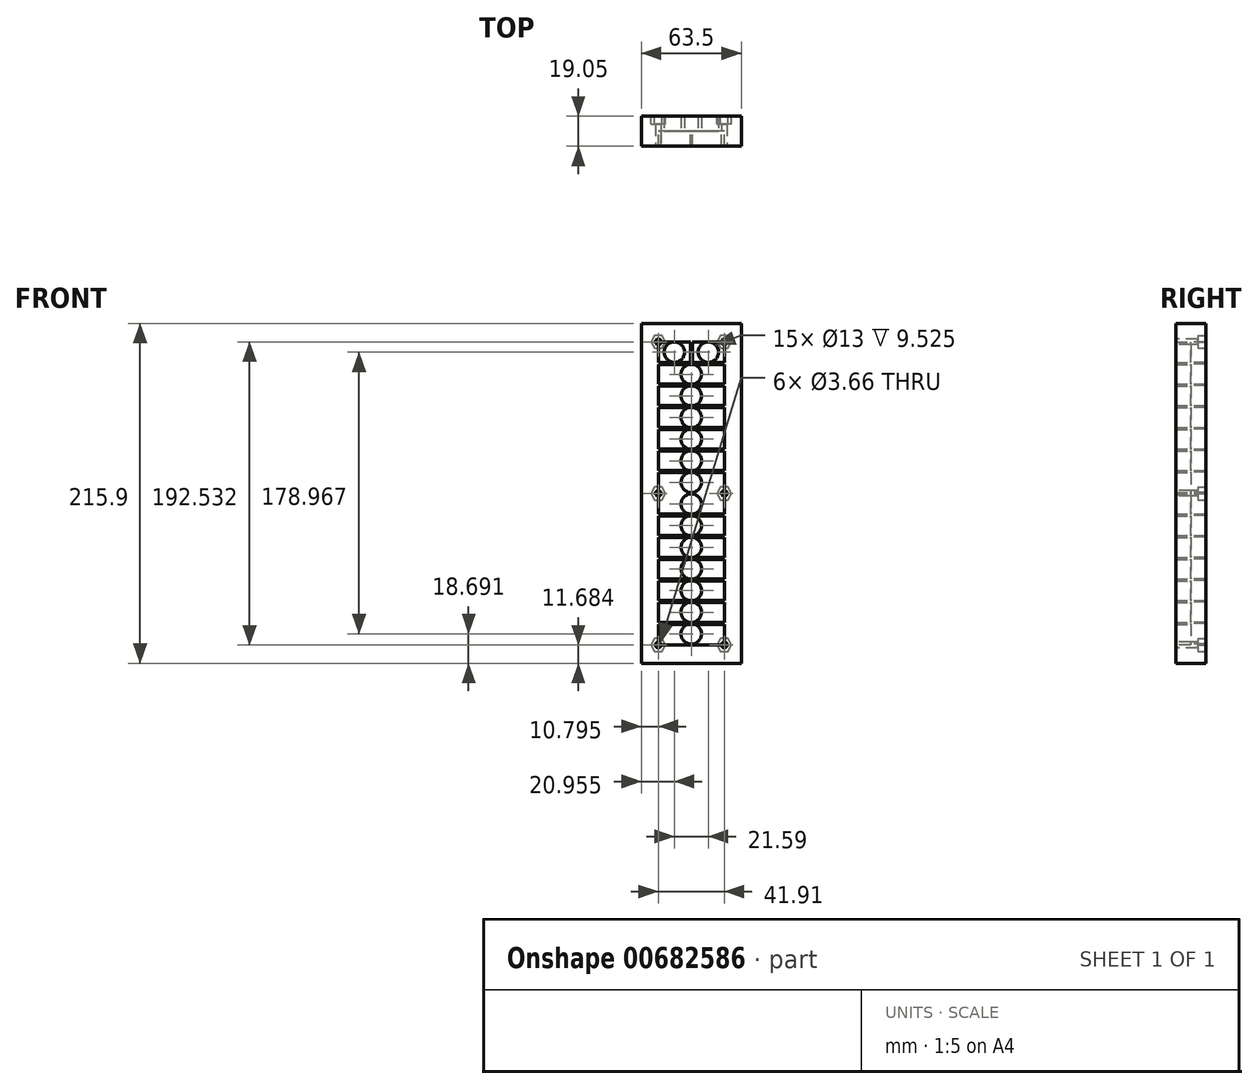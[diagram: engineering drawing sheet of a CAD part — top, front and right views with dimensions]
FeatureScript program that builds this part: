
annotation { "Feature Type Name" : "Feature", "Feature Type Description" : "" }
export const myFeature = defineFeature(function(context is Context, id is Id, definition is map)
    precondition{}
    {
        {
            var Q0;
            Q0=qCreatedBy(makeId("Front.planeOp"),FACE);
            var sketch = newSketch(context, id + "F0", { "sketchPlane" : qUnion([Q0])});
            skLineSegment(sketch, "E0.bottom", {"start": v(31.75, 107.95) * mm, "end": v(-31.75, 107.95) * mm});
            skLineSegment(sketch, "E0.top", {"start": v(31.75, -107.95) * mm, "end": v(-31.75, -107.95) * mm});
            skLineSegment(sketch, "E0.left", {"start": v(31.75, 107.95) * mm, "end": v(31.75, -107.95) * mm});
            skLineSegment(sketch, "E0.right", {"start": v(-31.75, 107.95) * mm, "end": v(-31.75, -107.95) * mm});
            skPoint(sketch, "E0.middle", {"position": v(0, 0) * mm});
            skSolve(sketch);
        }
        {
            var Q0;
            Q0=makeQuery(id+"F0.imprint","IMPRINT",FACE,{"disambiguationData":[TD([[makeQuery(id+"F0.imprint","IMPRINT",EDGE,{"derivedFrom":sQuery(id+"F0.wireOp",EDGE,"E0.bottom")}),1.0]])]});
            extrude(context, id + "F1", {"entities" : qUnion([Q0]), "depth" : 19.05 * mm, "offsetDistance" : 25.4 * mm});
        }
        {
            var Q0;
            Q0=makeQuery(id+"F1.opExtrude","CAP_FACE",FACE,{"disambiguationData":[OSD([sQuery(id+"F0.wireOp",EDGE,"E0.bottom"),sQuery(id+"F0.wireOp",EDGE,"E0.top"),sQuery(id+"F0.wireOp",EDGE,"E0.left"),sQuery(id+"F0.wireOp",EDGE,"E0.right")])],"isStart":false});
            var sketch = newSketch(context, id + "F2", { "sketchPlane" : qUnion([Q0])});
            skLineSegment(sketch, "E1.bottom", {"start": v(20.96, 96.27) * mm, "end": v(-20.95, 96.27) * mm});
            skLineSegment(sketch, "E1.top", {"start": v(20.95, -96.27) * mm, "end": v(-20.96, -96.27) * mm});
            skLineSegment(sketch, "E1.left", {"start": v(20.96, 96.27) * mm, "end": v(20.95, -96.27) * mm});
            skLineSegment(sketch, "E1.right", {"start": v(-20.95, 96.27) * mm, "end": v(-20.96, -96.27) * mm});
            skPoint(sketch, "E1.middle", {"position": v(0, 0) * mm});
            skSolve(sketch);
        }
        {
            var Q0;
            Q0 = qSketchRegion(id + "F2", true);
            extrude(context, id + "F3", {"entities" : qUnion([Q0]), "operationType" : NewBodyOperationType.REMOVE, "oppositeDirection" : true, "depth" : 9.52 * mm, "offsetDistance" : 25.4 * mm});
        }
        {
            var Q0;
            Q0=makeQuery(id+"F1.opExtrude","CAP_FACE",FACE,{"disambiguationData":[OSD([sQuery(id+"F0.wireOp",EDGE,"E0.bottom"),sQuery(id+"F0.wireOp",EDGE,"E0.top"),sQuery(id+"F0.wireOp",EDGE,"E0.left"),sQuery(id+"F0.wireOp",EDGE,"E0.right")])],"isStart":false});
            var sketch = newSketch(context, id + "F4", { "sketchPlane" : qUnion([Q0])});
            skPoint(sketch, "E2", {"position": v(-20.95, 96.27) * mm});
            skPoint(sketch, "E3", {"position": v(20.96, 96.27) * mm});
            skPoint(sketch, "E4", {"position": v(-20.96, -96.27) * mm});
            skPoint(sketch, "E5", {"position": v(20.95, -96.27) * mm});
            skPoint(sketch, "E6", {"position": v(-20.96, 0) * mm});
            skPoint(sketch, "E7", {"position": v(20.96, 0) * mm});
            skSolve(sketch);
        }
        {
            var Q0;
            Q0=sQuery(id+"F4.wireOp",VERTEX,"E4");
            var Q1;
            Q1=sQuery(id+"F4.wireOp",VERTEX,"E6");
            var Q2;
            Q2=sQuery(id+"F4.wireOp",VERTEX,"E7");
            var Q3;
            Q3=sQuery(id+"F4.wireOp",VERTEX,"E5");
            var Q4;
            Q4=sQuery(id+"F4.wireOp",VERTEX,"E2");
            var Q5;
            Q5=sQuery(id+"F4.wireOp",VERTEX,"E3");
            var Q6;
            Q6=makeQuery(id+"F1.opExtrude","SWEPT_BODY",BODY,{"disambiguationData":[OSD([sQuery(id+"F0.wireOp",EDGE,"E0.bottom"),sQuery(id+"F0.wireOp",EDGE,"E0.top"),sQuery(id+"F0.wireOp",EDGE,"E0.left"),sQuery(id+"F0.wireOp",EDGE,"E0.right")])]});
            hole(context, id + "F5", {"style" : HoleStyle.SIMPLE, "endStyle" : HoleEndStyle.BLIND, "standardTappedOrClearance" : lookupTablePath({ "standard" : "ANSI", "fit" : "Close", "size" : "#6", "type" : "Clearance" }), "standardBlindInLast" : lookupTablePath({ "fit" : "Close", "standard" : "ANSI", "size" : "#6", "type" : "Clearance" }), "holeDiameter" : 3.66 * mm, "majorDiameter" : 6.35 * mm, "holeDepth" : 19.05 * mm, "isTappedThrough" : true, "tappedDepth" : 12.7 * mm, "tapClearance" : 3, "locations" : qUnion([Q0, Q1, Q2, Q3, Q4, Q5]), "scope" : qUnion([Q6])});
        }
        {
            var Q0;
            Q0=makeQuery(id+"F1.opExtrude","CAP_FACE",FACE,{"disambiguationData":[OSD([sQuery(id+"F0.wireOp",EDGE,"E0.bottom"),sQuery(id+"F0.wireOp",EDGE,"E0.top"),sQuery(id+"F0.wireOp",EDGE,"E0.left"),sQuery(id+"F0.wireOp",EDGE,"E0.right")])],"isStart":true});
            var sketch = newSketch(context, id + "F6", { "sketchPlane" : qUnion([Q0])});
            skCircle(sketch, "E8.cCircle", {"center": v(-20.96, 96.27) * mm, "radius": 4.06 * mm, "construction": true});
            skLineSegment(sketch, "E8.0", {"start": v(-18.6, 100.33) * mm, "end": v(-16.26, 96.27) * mm});
            skLineSegment(sketch, "E8.1", {"start": v(-16.26, 96.27) * mm, "end": v(-18.6, 92.2) * mm});
            skLineSegment(sketch, "E8.2", {"start": v(-18.6, 92.2) * mm, "end": v(-23.3, 92.2) * mm});
            skLineSegment(sketch, "E8.3", {"start": v(-23.3, 92.2) * mm, "end": v(-25.65, 96.27) * mm});
            skLineSegment(sketch, "E8.4", {"start": v(-25.65, 96.27) * mm, "end": v(-23.3, 100.33) * mm});
            skLineSegment(sketch, "E8.5", {"start": v(-23.3, 100.33) * mm, "end": v(-18.6, 100.33) * mm});
            skPoint(sketch, "E8.0.midPoint", {"position": v(-17.44, 98.3) * mm});
            skLineSegment(sketch, "E9.0.1.0", {"start": v(-16.26, 0) * mm, "end": v(-18.6, -4.06) * mm});
            skLineSegment(sketch, "E9.0.1.1", {"start": v(-18.6, -4.06) * mm, "end": v(-23.3, -4.06) * mm});
            skLineSegment(sketch, "E9.0.1.2", {"start": v(-23.3, -4.06) * mm, "end": v(-25.65, 0) * mm});
            skLineSegment(sketch, "E9.0.1.3", {"start": v(-25.65, 0) * mm, "end": v(-23.3, 4.06) * mm});
            skLineSegment(sketch, "E9.0.1.4", {"start": v(-23.3, 4.06) * mm, "end": v(-18.6, 4.06) * mm});
            skLineSegment(sketch, "E9.0.1.5", {"start": v(-18.6, 4.06) * mm, "end": v(-16.26, 0) * mm});
            skLineSegment(sketch, "E9.0.2.0", {"start": v(-16.26, -96.27) * mm, "end": v(-18.6, -100.33) * mm});
            skLineSegment(sketch, "E9.0.2.1", {"start": v(-18.6, -100.33) * mm, "end": v(-23.3, -100.33) * mm});
            skLineSegment(sketch, "E9.0.2.2", {"start": v(-23.3, -100.33) * mm, "end": v(-25.65, -96.27) * mm});
            skLineSegment(sketch, "E9.0.2.3", {"start": v(-25.65, -96.27) * mm, "end": v(-23.3, -92.2) * mm});
            skLineSegment(sketch, "E9.0.2.4", {"start": v(-23.3, -92.2) * mm, "end": v(-18.6, -92.2) * mm});
            skLineSegment(sketch, "E9.0.2.5", {"start": v(-18.6, -92.2) * mm, "end": v(-16.26, -96.27) * mm});
            skLineSegment(sketch, "E9.1.0.0", {"start": v(25.65, 96.27) * mm, "end": v(23.3, 92.2) * mm});
            skLineSegment(sketch, "E9.1.0.1", {"start": v(23.3, 92.2) * mm, "end": v(18.6, 92.2) * mm});
            skLineSegment(sketch, "E9.1.0.2", {"start": v(18.6, 92.2) * mm, "end": v(16.26, 96.27) * mm});
            skLineSegment(sketch, "E9.1.0.3", {"start": v(16.26, 96.27) * mm, "end": v(18.6, 100.33) * mm});
            skLineSegment(sketch, "E9.1.0.4", {"start": v(18.6, 100.33) * mm, "end": v(23.3, 100.33) * mm});
            skLineSegment(sketch, "E9.1.0.5", {"start": v(23.3, 100.33) * mm, "end": v(25.65, 96.27) * mm});
            skLineSegment(sketch, "E9.1.1.0", {"start": v(25.65, 0) * mm, "end": v(23.3, -4.06) * mm});
            skLineSegment(sketch, "E9.1.1.1", {"start": v(23.3, -4.06) * mm, "end": v(18.6, -4.06) * mm});
            skLineSegment(sketch, "E9.1.1.2", {"start": v(18.6, -4.06) * mm, "end": v(16.26, 0) * mm});
            skLineSegment(sketch, "E9.1.1.3", {"start": v(16.26, 0) * mm, "end": v(18.6, 4.06) * mm});
            skLineSegment(sketch, "E9.1.1.4", {"start": v(18.6, 4.06) * mm, "end": v(23.3, 4.06) * mm});
            skLineSegment(sketch, "E9.1.1.5", {"start": v(23.3, 4.06) * mm, "end": v(25.65, 0) * mm});
            skLineSegment(sketch, "E9.1.2.0", {"start": v(25.65, -96.27) * mm, "end": v(23.3, -100.33) * mm});
            skLineSegment(sketch, "E9.1.2.1", {"start": v(23.3, -100.33) * mm, "end": v(18.6, -100.33) * mm});
            skLineSegment(sketch, "E9.1.2.2", {"start": v(18.6, -100.33) * mm, "end": v(16.26, -96.27) * mm});
            skLineSegment(sketch, "E9.1.2.3", {"start": v(16.26, -96.27) * mm, "end": v(18.6, -92.2) * mm});
            skLineSegment(sketch, "E9.1.2.4", {"start": v(18.6, -92.2) * mm, "end": v(23.3, -92.2) * mm});
            skLineSegment(sketch, "E9.1.2.5", {"start": v(23.3, -92.2) * mm, "end": v(25.65, -96.27) * mm});
            skLineSegment(sketch, "E9.direction1", {"start": v(-18.6, 92.2) * mm, "end": v(23.3, 92.2) * mm, "construction": true});
            skLineSegment(sketch, "E9.direction2", {"start": v(-18.6, 92.2) * mm, "end": v(-18.6, -4.06) * mm, "construction": true});
            skSolve(sketch);
        }
        {
            var Q0;
            Q0=makeQuery(id+"F6.imprint","IMPRINT",FACE,{"disambiguationData":[TD([[makeQuery(id+"F6.imprint","IMPRINT",EDGE,{"derivedFrom":sQuery(id+"F6.wireOp",EDGE,"E8.0")}),-1.0]])]});
            var Q1;
            Q1=makeQuery(id+"F6.imprint","IMPRINT",FACE,{"disambiguationData":[TD([[makeQuery(id+"F6.imprint","IMPRINT",EDGE,{"derivedFrom":sQuery(id+"F6.wireOp",EDGE,"E9.1.0.0")}),-1.0]])]});
            var Q2;
            Q2=makeQuery(id+"F6.imprint","IMPRINT",FACE,{"disambiguationData":[TD([[makeQuery(id+"F6.imprint","IMPRINT",EDGE,{"derivedFrom":sQuery(id+"F6.wireOp",EDGE,"E9.0.1.0")}),-1.0]])]});
            var Q3;
            Q3=makeQuery(id+"F6.imprint","IMPRINT",FACE,{"disambiguationData":[TD([[makeQuery(id+"F6.imprint","IMPRINT",EDGE,{"derivedFrom":sQuery(id+"F6.wireOp",EDGE,"E9.1.1.0")}),-1.0]])]});
            var Q4;
            Q4=makeQuery(id+"F6.imprint","IMPRINT",FACE,{"disambiguationData":[TD([[makeQuery(id+"F6.imprint","IMPRINT",EDGE,{"derivedFrom":sQuery(id+"F6.wireOp",EDGE,"E9.0.2.0")}),-1.0]])]});
            var Q5;
            Q5=makeQuery(id+"F6.imprint","IMPRINT",FACE,{"disambiguationData":[TD([[makeQuery(id+"F6.imprint","IMPRINT",EDGE,{"derivedFrom":sQuery(id+"F6.wireOp",EDGE,"E9.1.2.0")}),-1.0]])]});
            extrude(context, id + "F7", {"entities" : qUnion([Q0, Q1, Q2, Q3, Q4, Q5]), "operationType" : NewBodyOperationType.REMOVE, "oppositeDirection" : true, "depth" : 5.08 * mm, "offsetDistance" : 25.4 * mm});
        }
        {
            var Q0;
            Q0=makeQuery(id+"F3.boolean.opBoolean","COPY",FACE,{"derivedFrom":makeQuery(id+"F3.opExtrude","CAP_FACE",FACE,{"disambiguationData":[OSD([sQuery(id+"F2.wireOp",EDGE,"E1.bottom"),sQuery(id+"F2.wireOp",EDGE,"E1.top"),sQuery(id+"F2.wireOp",EDGE,"E1.left"),sQuery(id+"F2.wireOp",EDGE,"E1.right")])],"isStart":false})});
            var sketch = newSketch(context, id + "F8", { "sketchPlane" : qUnion([Q0])});
            skLineSegment(sketch, "E10.bottom", {"start": v(20.96, 0.64) * mm, "end": v(-20.96, 0.64) * mm});
            skLineSegment(sketch, "E10.top", {"start": v(20.96, -0.64) * mm, "end": v(-20.96, -0.64) * mm});
            skLineSegment(sketch, "E10.left", {"start": v(20.96, 0.64) * mm, "end": v(20.96, -0.64) * mm});
            skLineSegment(sketch, "E10.right", {"start": v(-20.96, 0.64) * mm, "end": v(-20.96, -0.64) * mm});
            skPoint(sketch, "E10.middle", {"position": v(0, 0) * mm});
            skLineSegment(sketch, "E11.0.1.0", {"start": v(20.96, 13.12) * mm, "end": v(-20.96, 13.12) * mm});
            skLineSegment(sketch, "E11.0.1.1", {"start": v(20.96, 14.39) * mm, "end": v(20.96, 13.12) * mm});
            skLineSegment(sketch, "E11.0.1.2", {"start": v(20.96, 14.39) * mm, "end": v(-20.96, 14.39) * mm});
            skLineSegment(sketch, "E11.0.1.3", {"start": v(-20.96, 14.39) * mm, "end": v(-20.96, 13.12) * mm});
            skLineSegment(sketch, "E11.0.2.0", {"start": v(20.96, 26.87) * mm, "end": v(-20.96, 26.87) * mm});
            skLineSegment(sketch, "E11.0.2.1", {"start": v(20.96, 28.14) * mm, "end": v(20.96, 26.87) * mm});
            skLineSegment(sketch, "E11.0.2.2", {"start": v(20.96, 28.14) * mm, "end": v(-20.96, 28.14) * mm});
            skLineSegment(sketch, "E11.0.2.3", {"start": v(-20.96, 28.14) * mm, "end": v(-20.96, 26.87) * mm});
            skLineSegment(sketch, "E11.0.3.0", {"start": v(20.96, 40.62) * mm, "end": v(-20.96, 40.62) * mm});
            skLineSegment(sketch, "E11.0.3.1", {"start": v(20.96, 41.9) * mm, "end": v(20.96, 40.62) * mm});
            skLineSegment(sketch, "E11.0.3.2", {"start": v(20.96, 41.9) * mm, "end": v(-20.96, 41.9) * mm});
            skLineSegment(sketch, "E11.0.3.3", {"start": v(-20.96, 41.9) * mm, "end": v(-20.96, 40.62) * mm});
            skLineSegment(sketch, "E11.0.4.0", {"start": v(20.96, 54.37) * mm, "end": v(-20.96, 54.37) * mm});
            skLineSegment(sketch, "E11.0.4.1", {"start": v(20.96, 55.64) * mm, "end": v(20.96, 54.37) * mm});
            skLineSegment(sketch, "E11.0.4.2", {"start": v(20.96, 55.64) * mm, "end": v(-20.96, 55.64) * mm});
            skLineSegment(sketch, "E11.0.4.3", {"start": v(-20.96, 55.64) * mm, "end": v(-20.96, 54.37) * mm});
            skLineSegment(sketch, "E11.0.5.0", {"start": v(20.96, 68.13) * mm, "end": v(-20.96, 68.13) * mm});
            skLineSegment(sketch, "E11.0.5.1", {"start": v(20.96, 69.4) * mm, "end": v(20.96, 68.13) * mm});
            skLineSegment(sketch, "E11.0.5.2", {"start": v(20.96, 69.4) * mm, "end": v(-20.96, 69.4) * mm});
            skLineSegment(sketch, "E11.0.5.3", {"start": v(-20.96, 69.4) * mm, "end": v(-20.96, 68.13) * mm});
            skLineSegment(sketch, "E11.0.6.0", {"start": v(20.96, 81.88) * mm, "end": v(-20.96, 81.88) * mm});
            skLineSegment(sketch, "E11.0.6.1", {"start": v(20.96, 83.15) * mm, "end": v(20.96, 81.88) * mm});
            skLineSegment(sketch, "E11.0.6.2", {"start": v(20.96, 83.15) * mm, "end": v(-20.96, 83.15) * mm});
            skLineSegment(sketch, "E11.0.6.3", {"start": v(-20.96, 83.15) * mm, "end": v(-20.96, 81.88) * mm});
            skLineSegment(sketch, "E11.direction1", {"start": v(-20.96, -0.64) * mm, "end": v(4.44, -0.64) * mm, "construction": true});
            skLineSegment(sketch, "E11.direction2", {"start": v(-20.96, -0.64) * mm, "end": v(-20.96, 13.12) * mm, "construction": true});
            skLineSegment(sketch, "E12", {"start": v(20.96, 0) * mm, "end": v(0, 0) * mm});
            skLineSegment(sketch, "E13.MirrorCS", {"start": v(-20.96, -14.39) * mm, "end": v(-20.96, -13.12) * mm});
            skLineSegment(sketch, "E14.MirrorCS", {"start": v(20.96, -14.39) * mm, "end": v(-20.96, -14.39) * mm});
            skLineSegment(sketch, "E15.MirrorCS", {"start": v(20.96, -13.12) * mm, "end": v(-20.96, -13.12) * mm});
            skLineSegment(sketch, "E16.MirrorCS", {"start": v(20.96, -14.39) * mm, "end": v(20.96, -13.12) * mm});
            skLineSegment(sketch, "E17.MirrorCS", {"start": v(20.96, -26.87) * mm, "end": v(-20.96, -26.87) * mm});
            skLineSegment(sketch, "E18.MirrorCS", {"start": v(20.96, -28.14) * mm, "end": v(-20.96, -28.14) * mm});
            skLineSegment(sketch, "E19.MirrorCS", {"start": v(20.96, -28.14) * mm, "end": v(20.96, -26.87) * mm});
            skLineSegment(sketch, "E20.MirrorCS", {"start": v(-20.96, -28.14) * mm, "end": v(-20.96, -26.87) * mm});
            skLineSegment(sketch, "E21.MirrorCS", {"start": v(20.96, -41.9) * mm, "end": v(-20.96, -41.9) * mm});
            skLineSegment(sketch, "E22.MirrorCS", {"start": v(20.96, -40.62) * mm, "end": v(-20.96, -40.62) * mm});
            skLineSegment(sketch, "E23.MirrorCS", {"start": v(-20.96, -41.9) * mm, "end": v(-20.96, -40.62) * mm});
            skLineSegment(sketch, "E24.MirrorCS", {"start": v(20.96, -41.9) * mm, "end": v(20.96, -40.62) * mm});
            skLineSegment(sketch, "E25.MirrorCS", {"start": v(20.96, -55.64) * mm, "end": v(-20.96, -55.64) * mm});
            skLineSegment(sketch, "E26.MirrorCS", {"start": v(20.96, -54.37) * mm, "end": v(-20.96, -54.37) * mm});
            skLineSegment(sketch, "E27.MirrorCS", {"start": v(-20.96, -55.64) * mm, "end": v(-20.96, -54.37) * mm});
            skLineSegment(sketch, "E28.MirrorCS", {"start": v(20.96, -55.64) * mm, "end": v(20.96, -54.37) * mm});
            skLineSegment(sketch, "E29.MirrorCS", {"start": v(20.96, -69.4) * mm, "end": v(-20.96, -69.4) * mm});
            skLineSegment(sketch, "E30.MirrorCS", {"start": v(20.96, -68.13) * mm, "end": v(-20.96, -68.13) * mm});
            skLineSegment(sketch, "E31.MirrorCS", {"start": v(-20.96, -69.4) * mm, "end": v(-20.96, -68.13) * mm});
            skLineSegment(sketch, "E32.MirrorCS", {"start": v(20.96, -69.4) * mm, "end": v(20.96, -68.13) * mm});
            skLineSegment(sketch, "E33.MirrorCS", {"start": v(20.96, -83.15) * mm, "end": v(-20.96, -83.15) * mm});
            skLineSegment(sketch, "E34.MirrorCS", {"start": v(20.96, -81.88) * mm, "end": v(-20.96, -81.88) * mm});
            skLineSegment(sketch, "E35.MirrorCS", {"start": v(20.96, -83.15) * mm, "end": v(20.96, -81.88) * mm});
            skLineSegment(sketch, "E36.MirrorCS", {"start": v(-20.96, -83.15) * mm, "end": v(-20.96, -81.88) * mm});
            skSolve(sketch);
        }
        {
            var Q0;
            Q0=makeQuery(id+"F8.imprint","IMPRINT",FACE,{"disambiguationData":[TD([[makeQuery(id+"F8.imprint","IMPRINT",EDGE,{"derivedFrom":sQuery(id+"F8.wireOp",EDGE,"E11.0.6.0")}),-1.0]])]});
            var Q1;
            Q1=makeQuery(id+"F8.imprint","IMPRINT",FACE,{"disambiguationData":[TD([[makeQuery(id+"F8.imprint","IMPRINT",EDGE,{"derivedFrom":sQuery(id+"F8.wireOp",EDGE,"E11.0.5.0")}),-1.0]])]});
            var Q2;
            Q2=makeQuery(id+"F8.imprint","IMPRINT",FACE,{"disambiguationData":[TD([[makeQuery(id+"F8.imprint","IMPRINT",EDGE,{"derivedFrom":sQuery(id+"F8.wireOp",EDGE,"E11.0.4.0")}),-1.0]])]});
            var Q3;
            Q3=makeQuery(id+"F8.imprint","IMPRINT",FACE,{"disambiguationData":[TD([[makeQuery(id+"F8.imprint","IMPRINT",EDGE,{"derivedFrom":sQuery(id+"F8.wireOp",EDGE,"E11.0.3.0")}),-1.0]])]});
            var Q4;
            Q4=makeQuery(id+"F8.imprint","IMPRINT",FACE,{"disambiguationData":[TD([[makeQuery(id+"F8.imprint","IMPRINT",EDGE,{"derivedFrom":sQuery(id+"F8.wireOp",EDGE,"E11.0.2.0")}),-1.0]])]});
            var Q5;
            Q5=makeQuery(id+"F8.imprint","IMPRINT",FACE,{"disambiguationData":[TD([[makeQuery(id+"F8.imprint","IMPRINT",EDGE,{"derivedFrom":sQuery(id+"F8.wireOp",EDGE,"E11.0.1.0")}),-1.0]])]});
            var Q6;
            {var subQ0=sQuery(id+"F8.wireOp",EDGE,"E10.bottom");var subQ1=makeQuery(id+"F3.boolean.opBoolean","COPY",FACE,{"derivedFrom":makeQuery(id+"F3.opExtrude","CAP_FACE",FACE,{"disambiguationData":[OSD([sQuery(id+"F2.wireOp",EDGE,"E1.bottom"),sQuery(id+"F2.wireOp",EDGE,"E1.top"),sQuery(id+"F2.wireOp",EDGE,"E1.left"),sQuery(id+"F2.wireOp",EDGE,"E1.right")])],"isStart":false})});var subQ2=makeQuery(id+"F5.hole-2.boolean.opBoolean","INTERSECT",EDGE,{"derivedFrom":[subQ1,makeQuery(id+"F5.hole-2.opRevolve","SWEPT_FACE",FACE,{"disambiguationData":[OSD([sQuery(id+"F5.hole-2.sketch.wireOp",EDGE,"core_line_2")])]})]});var subQ3=makeQuery(id+"F8.imprint","INTERSECT",VERTEX,{"derivedFrom":[subQ2,subQ0]});Q6=makeQuery(id+"F8.imprint","IMPRINT",FACE,{"disambiguationData":[TD([[makeQuery(id+"F8.imprint","IMPRINT",EDGE,{"disambiguationData":[TD([[subQ3,-1.0]])],"derivedFrom":subQ0}),1.0]])]});}
            var Q7;
            Q7=makeQuery(id+"F8.imprint","IMPRINT",FACE,{"disambiguationData":[TD([[makeQuery(id+"F8.imprint","IMPRINT",EDGE,{"derivedFrom":sQuery(id+"F8.wireOp",EDGE,"E13.MirrorCS")}),1.0]])]});
            var Q8;
            Q8=makeQuery(id+"F8.imprint","IMPRINT",FACE,{"disambiguationData":[TD([[makeQuery(id+"F8.imprint","IMPRINT",EDGE,{"derivedFrom":sQuery(id+"F8.wireOp",EDGE,"E17.MirrorCS")}),1.0]])]});
            var Q9;
            Q9=makeQuery(id+"F8.imprint","IMPRINT",FACE,{"disambiguationData":[TD([[makeQuery(id+"F8.imprint","IMPRINT",EDGE,{"derivedFrom":sQuery(id+"F8.wireOp",EDGE,"E21.MirrorCS")}),-1.0]])]});
            var Q10;
            Q10=makeQuery(id+"F8.imprint","IMPRINT",FACE,{"disambiguationData":[TD([[makeQuery(id+"F8.imprint","IMPRINT",EDGE,{"derivedFrom":sQuery(id+"F8.wireOp",EDGE,"E25.MirrorCS")}),-1.0]])]});
            var Q11;
            Q11=makeQuery(id+"F8.imprint","IMPRINT",FACE,{"disambiguationData":[TD([[makeQuery(id+"F8.imprint","IMPRINT",EDGE,{"derivedFrom":sQuery(id+"F8.wireOp",EDGE,"E29.MirrorCS")}),-1.0]])]});
            var Q12;
            Q12=makeQuery(id+"F8.imprint","IMPRINT",FACE,{"disambiguationData":[TD([[makeQuery(id+"F8.imprint","IMPRINT",EDGE,{"derivedFrom":sQuery(id+"F8.wireOp",EDGE,"E33.MirrorCS")}),-1.0]])]});
            var Q13;
            Q13=makeQuery(id+"F1.opExtrude","CAP_FACE",FACE,{"disambiguationData":[OSD([sQuery(id+"F0.wireOp",EDGE,"E0.bottom"),sQuery(id+"F0.wireOp",EDGE,"E0.top"),sQuery(id+"F0.wireOp",EDGE,"E0.left"),sQuery(id+"F0.wireOp",EDGE,"E0.right")])],"isStart":false});
            extrude(context, id + "F9", {"entities" : qUnion([Q0, Q1, Q2, Q3, Q4, Q5, Q6, Q7, Q8, Q9, Q10, Q11, Q12]), "operationType" : NewBodyOperationType.ADD, "endBound" : BoundingType.UP_TO_SURFACE, "depth" : 25.4 * mm, "endBoundEntityFace" : qUnion([Q13]), "offsetDistance" : 25.4 * mm});
        }
        {
            var Q0;
            {var subQ0=sQuery(id+"F2.wireOp",EDGE,"E1.right");var subQ1=sQuery(id+"F2.wireOp",EDGE,"E1.left");var subQ2=sQuery(id+"F2.wireOp",EDGE,"E1.bottom");Q0=makeQuery(id+"F9.boolean.opBoolean","SPLIT",FACE,{"disambiguationData":[TD([makeQuery(id+"F3.boolean.opBoolean","COPY",FACE,{"derivedFrom":makeQuery(id+"F3.opExtrude","SWEPT_FACE",FACE,{"disambiguationData":[OSD([subQ2])]})})])],"derivedFrom":makeQuery(id+"F3.boolean.opBoolean","COPY",FACE,{"derivedFrom":makeQuery(id+"F3.opExtrude","CAP_FACE",FACE,{"disambiguationData":[OSD([subQ2,sQuery(id+"F2.wireOp",EDGE,"E1.top"),subQ1,subQ0])],"isStart":false})})});}
            var sketch = newSketch(context, id + "F10", { "sketchPlane" : qUnion([Q0])});
            skLineSegment(sketch, "E37.bottom", {"start": v(0, 83.15) * mm, "end": v(0.64, 83.15) * mm});
            skLineSegment(sketch, "E37.top", {"start": v(0, 96.27) * mm, "end": v(0.64, 96.27) * mm});
            skLineSegment(sketch, "E37.left", {"start": v(0, 83.15) * mm, "end": v(0, 96.27) * mm});
            skLineSegment(sketch, "E37.right", {"start": v(0.64, 83.15) * mm, "end": v(0.64, 96.27) * mm});
            skLineSegment(sketch, "E38.bottom", {"start": v(0, 83.15) * mm, "end": v(-0.63, 83.15) * mm});
            skLineSegment(sketch, "E38.top", {"start": v(0, 96.27) * mm, "end": v(-0.63, 96.27) * mm});
            skLineSegment(sketch, "E38.right", {"start": v(-0.63, 83.15) * mm, "end": v(-0.63, 96.27) * mm});
            skSolve(sketch);
        }
        {
            var Q0;
            Q0=makeQuery(id+"F10.imprint","IMPRINT",FACE,{"disambiguationData":[TD([[makeQuery(id+"F10.imprint","IMPRINT",EDGE,{"derivedFrom":sQuery(id+"F10.wireOp",EDGE,"E38.bottom")}),-1.0]])]});
            var Q1;
            Q1=makeQuery(id+"F10.imprint","IMPRINT",FACE,{"disambiguationData":[TD([[makeQuery(id+"F10.imprint","IMPRINT",EDGE,{"derivedFrom":sQuery(id+"F10.wireOp",EDGE,"E37.bottom")}),-1.0]])]});
            var Q2;
            {var subQ0=sQuery(id+"F0.wireOp",EDGE,"E0.right");var subQ1=sQuery(id+"F0.wireOp",EDGE,"E0.left");var subQ2=sQuery(id+"F0.wireOp",EDGE,"E0.top");var subQ3=sQuery(id+"F0.wireOp",EDGE,"E0.bottom");Q2=makeQuery(id+"F9.boolean.opBoolean","MERGE",FACE,{"derivedFrom":[makeQuery(id+"F1.opExtrude","CAP_FACE",FACE,{"disambiguationData":[OSD([subQ3,subQ2,subQ1,subQ0])],"isStart":false}),makeQuery(id+"F9.opExtrude","CAP_FACE",FACE,{"disambiguationData":[OSD([subQ3,subQ2,subQ1,subQ0]),OD(1.0)],"isStart":false}),makeQuery(id+"F9.opExtrude","CAP_FACE",FACE,{"disambiguationData":[OSD([subQ3,subQ2,subQ1,subQ0]),OD(2.0)],"isStart":false}),makeQuery(id+"F9.opExtrude","CAP_FACE",FACE,{"disambiguationData":[OSD([subQ3,subQ2,subQ1,subQ0]),OD(3.0)],"isStart":false}),makeQuery(id+"F9.opExtrude","CAP_FACE",FACE,{"disambiguationData":[OSD([subQ3,subQ2,subQ1,subQ0]),OD(4.0)],"isStart":false}),makeQuery(id+"F9.opExtrude","CAP_FACE",FACE,{"disambiguationData":[OSD([subQ3,subQ2,subQ1,subQ0]),OD(5.0)],"isStart":false}),makeQuery(id+"F9.opExtrude","CAP_FACE",FACE,{"disambiguationData":[OSD([subQ3,subQ2,subQ1,subQ0]),OD(6.0)],"isStart":false}),makeQuery(id+"F9.opExtrude","CAP_FACE",FACE,{"disambiguationData":[OSD([subQ3,subQ2,subQ1,subQ0]),OD(7.0)],"isStart":false}),makeQuery(id+"F9.opExtrude","CAP_FACE",FACE,{"disambiguationData":[OSD([subQ3,subQ2,subQ1,subQ0]),OD(8.0)],"isStart":false}),makeQuery(id+"F9.opExtrude","CAP_FACE",FACE,{"disambiguationData":[OSD([subQ3,subQ2,subQ1,subQ0]),OD(9.0)],"isStart":false}),makeQuery(id+"F9.opExtrude","CAP_FACE",FACE,{"disambiguationData":[OSD([subQ3,subQ2,subQ1,subQ0]),OD(10.0)],"isStart":false}),makeQuery(id+"F9.opExtrude","CAP_FACE",FACE,{"disambiguationData":[OSD([subQ3,subQ2,subQ1,subQ0]),OD(11.0)],"isStart":false}),makeQuery(id+"F9.opExtrude","CAP_FACE",FACE,{"disambiguationData":[OSD([subQ3,subQ2,subQ1,subQ0]),OD(12.0)],"isStart":false})]});}
            extrude(context, id + "F11", {"entities" : qUnion([Q0, Q1]), "operationType" : NewBodyOperationType.ADD, "endBound" : BoundingType.UP_TO_SURFACE, "depth" : 25.4 * mm, "endBoundEntityFace" : qUnion([Q2]), "offsetDistance" : 25.4 * mm});
        }
        {
            var Q0;
            {var subQ1=sQuery(id+"F2.wireOp",EDGE,"E1.right");var subQ2=makeQuery(id+"F3.boolean.opBoolean","COPY",FACE,{"derivedFrom":makeQuery(id+"F3.opExtrude","SWEPT_FACE",FACE,{"disambiguationData":[OSD([subQ1])]})});var subQ4=sQuery(id+"F2.wireOp",EDGE,"E1.bottom");var subQ5=makeQuery(id+"F3.boolean.opBoolean","COPY",FACE,{"derivedFrom":makeQuery(id+"F3.opExtrude","SWEPT_FACE",FACE,{"disambiguationData":[OSD([subQ4])]})});var subQ6=sQuery(id+"F2.wireOp",EDGE,"E1.left");Q0=makeQuery(id+"F11.boolean.opBoolean","SPLIT",FACE,{"disambiguationData":[TD([subQ2])],"derivedFrom":makeQuery(id+"F9.boolean.opBoolean","SPLIT",FACE,{"disambiguationData":[TD([subQ5])],"derivedFrom":makeQuery(id+"F3.boolean.opBoolean","COPY",FACE,{"derivedFrom":makeQuery(id+"F3.opExtrude","CAP_FACE",FACE,{"disambiguationData":[OSD([subQ4,sQuery(id+"F2.wireOp",EDGE,"E1.top"),subQ6,subQ1])],"isStart":false})})})});}
            var sketch = newSketch(context, id + "F12", { "sketchPlane" : qUnion([Q0])});
            skCircle(sketch, "E39", {"center": v(-10.8, 89.7) * mm, "radius": 6.5 * mm});
            skPoint(sketch, "E39.centerSnap0", {"position": v(-10.8, 83.15) * mm});
            skPoint(sketch, "E39.centerSnap1", {"position": v(-0.63, 89.7) * mm});
            skSolve(sketch);
        }
        {
            var Q0;
            Q0=makeQuery(id+"F12.imprint","IMPRINT",FACE,{"disambiguationData":[TD([[makeQuery(id+"F12.imprint","IMPRINT",EDGE,{"derivedFrom":sQuery(id+"F12.wireOp",EDGE,"E39")}),1.0]])]});
            extrude(context, id + "F13", {"entities" : qUnion([Q0]), "operationType" : NewBodyOperationType.REMOVE, "oppositeDirection" : true, "depth" : 25.4 * mm, "offsetDistance" : 25.4 * mm});
        }
        {
            var Q0;
            {var subQ1=sQuery(id+"F2.wireOp",EDGE,"E1.left");var subQ2=makeQuery(id+"F3.boolean.opBoolean","COPY",FACE,{"derivedFrom":makeQuery(id+"F3.opExtrude","SWEPT_FACE",FACE,{"disambiguationData":[OSD([subQ1])]})});var subQ4=sQuery(id+"F2.wireOp",EDGE,"E1.bottom");var subQ5=makeQuery(id+"F3.boolean.opBoolean","COPY",FACE,{"derivedFrom":makeQuery(id+"F3.opExtrude","SWEPT_FACE",FACE,{"disambiguationData":[OSD([subQ4])]})});var subQ6=sQuery(id+"F2.wireOp",EDGE,"E1.right");Q0=makeQuery(id+"F11.boolean.opBoolean","SPLIT",FACE,{"disambiguationData":[TD([subQ2])],"derivedFrom":makeQuery(id+"F9.boolean.opBoolean","SPLIT",FACE,{"disambiguationData":[TD([subQ5])],"derivedFrom":makeQuery(id+"F3.boolean.opBoolean","COPY",FACE,{"derivedFrom":makeQuery(id+"F3.opExtrude","CAP_FACE",FACE,{"disambiguationData":[OSD([subQ4,sQuery(id+"F2.wireOp",EDGE,"E1.top"),subQ1,subQ6])],"isStart":false})})})});}
            var sketch = newSketch(context, id + "F14", { "sketchPlane" : qUnion([Q0])});
            skCircle(sketch, "E40", {"center": v(10.8, 89.7) * mm, "radius": 6.5 * mm});
            skPoint(sketch, "E40.centerSnap0", {"position": v(10.8, 83.15) * mm});
            skPoint(sketch, "E40.centerSnap1", {"position": v(0.64, 89.7) * mm});
            skSolve(sketch);
        }
        {
            var Q0;
            Q0=makeQuery(id+"F14.imprint","IMPRINT",FACE,{"disambiguationData":[TD([[makeQuery(id+"F14.imprint","IMPRINT",EDGE,{"derivedFrom":sQuery(id+"F14.wireOp",EDGE,"E40")}),1.0]])]});
            extrude(context, id + "F15", {"entities" : qUnion([Q0]), "operationType" : NewBodyOperationType.REMOVE, "oppositeDirection" : true, "depth" : 25.4 * mm, "offsetDistance" : 25.4 * mm});
        }
        {
            var Q0;
            {var subQ0=sQuery(id+"F2.wireOp",EDGE,"E1.left");var subQ1=sQuery(id+"F2.wireOp",EDGE,"E1.right");Q0=makeQuery(id+"F9.boolean.opBoolean","SPLIT",FACE,{"disambiguationData":[TD([makeQuery(id+"F9.opExtrude","SWEPT_FACE",FACE,{"disambiguationData":[OSD([sQuery(id+"F8.wireOp",EDGE,"E11.0.5.2")])]})])],"derivedFrom":makeQuery(id+"F3.boolean.opBoolean","COPY",FACE,{"derivedFrom":makeQuery(id+"F3.opExtrude","CAP_FACE",FACE,{"disambiguationData":[OSD([sQuery(id+"F2.wireOp",EDGE,"E1.bottom"),sQuery(id+"F2.wireOp",EDGE,"E1.top"),subQ0,subQ1])],"isStart":false})})});}
            var sketch = newSketch(context, id + "F16", { "sketchPlane" : qUnion([Q0])});
            skCircle(sketch, "E41", {"center": v(0, 75.64) * mm, "radius": 6.5 * mm});
            skPoint(sketch, "E41.centerSnap0", {"position": v(-20.96, 75.64) * mm});
            skPoint(sketch, "E41.centerSnap1", {"position": v(0, 81.88) * mm});
            skCircle(sketch, "E42.0.1.0", {"center": v(0, 61.9) * mm, "radius": 6.5 * mm});
            skCircle(sketch, "E42.0.2.0", {"center": v(0, 48.15) * mm, "radius": 6.5 * mm});
            skCircle(sketch, "E42.0.3.0", {"center": v(0, 34.41) * mm, "radius": 6.5 * mm});
            skCircle(sketch, "E42.0.4.0", {"center": v(0, 20.67) * mm, "radius": 6.5 * mm});
            skCircle(sketch, "E42.0.5.0", {"center": v(0, 6.93) * mm, "radius": 6.5 * mm});
            skCircle(sketch, "E42.0.6.0", {"center": v(0, -6.81) * mm, "radius": 6.5 * mm});
            skCircle(sketch, "E42.0.7.0", {"center": v(0, -20.55) * mm, "radius": 6.5 * mm});
            skCircle(sketch, "E42.0.8.0", {"center": v(0, -34.3) * mm, "radius": 6.5 * mm});
            skCircle(sketch, "E42.0.9.0", {"center": v(0, -48.04) * mm, "radius": 6.5 * mm});
            skCircle(sketch, "E42.0.10.0", {"center": v(0, -61.78) * mm, "radius": 6.5 * mm});
            skCircle(sketch, "E42.0.11.0", {"center": v(0, -75.52) * mm, "radius": 6.5 * mm});
            skCircle(sketch, "E42.0.12.0", {"center": v(0, -89.26) * mm, "radius": 6.5 * mm});
            skLineSegment(sketch, "E42.direction1", {"start": v(0, 75.64) * mm, "end": v(25.4, 75.64) * mm, "construction": true});
            skLineSegment(sketch, "E42.direction2", {"start": v(0, 75.64) * mm, "end": v(0, 61.9) * mm, "construction": true});
            skSolve(sketch);
        }
        {
            var Q0;
            Q0 = qSketchRegion(id + "F16", true);
            extrude(context, id + "F17", {"entities" : qUnion([Q0]), "operationType" : NewBodyOperationType.REMOVE, "oppositeDirection" : true, "depth" : 25.4 * mm, "offsetDistance" : 25.4 * mm});
        }
    });
